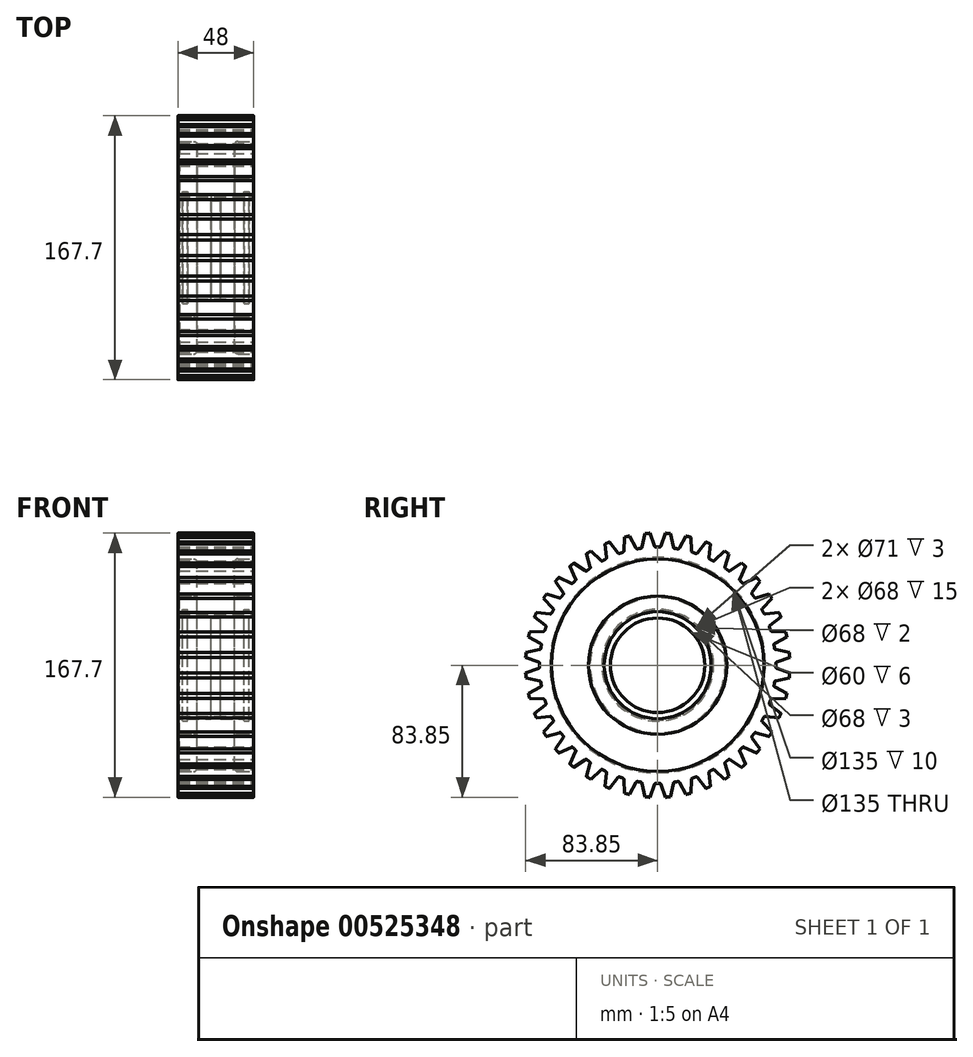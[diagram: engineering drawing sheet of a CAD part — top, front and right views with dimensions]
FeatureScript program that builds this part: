
annotation { "Feature Type Name" : "Feature", "Feature Type Description" : "" }
export const myFeature = defineFeature(function(context is Context, id is Id, definition is map)
    precondition{}
    {
        {
            var Q0;
            Q0=qCreatedBy(makeId("Front.planeOp"),FACE);
            var sketch = newSketch(context, id + "F0", { "sketchPlane" : qUnion([Q0])});
            skLineSegment(sketch, "E0.bottom", {"start": v(0, 0) * mm, "end": v(-24, 0) * mm, "construction": true});
            skLineSegment(sketch, "E0.top", {"start": v(0, 84) * mm, "end": v(-24, 84) * mm});
            skLineSegment(sketch, "E0.left", {"start": v(0, 0) * mm, "end": v(0, 84) * mm, "construction": true});
            skLineSegment(sketch, "E0.right", {"start": v(-24, 34) * mm, "end": v(-24, 44) * mm});
            skLineSegment(sketch, "E1", {"start": v(-24, 34) * mm, "end": v(-21, 34) * mm});
            skLineSegment(sketch, "E2", {"start": v(-21, 34) * mm, "end": v(-21, 35.5) * mm});
            skLineSegment(sketch, "E3", {"start": v(-21, 35.5) * mm, "end": v(-18, 35.5) * mm});
            skLineSegment(sketch, "E4", {"start": v(-18, 35.5) * mm, "end": v(-18, 34) * mm});
            skLineSegment(sketch, "E5", {"start": v(-18, 34) * mm, "end": v(-3, 34) * mm});
            skLineSegment(sketch, "E6", {"start": v(-3, 34) * mm, "end": v(-3, 30) * mm});
            skLineSegment(sketch, "E7", {"start": v(-3, 30) * mm, "end": v(0, 30) * mm});
            skLineSegment(sketch, "E8.bottom", {"start": v(-24, 44) * mm, "end": v(-14, 44) * mm});
            skLineSegment(sketch, "E8.top", {"start": v(-24, 67.5) * mm, "end": v(-14, 67.5) * mm});
            skLineSegment(sketch, "E8.right", {"start": v(-12, 65.5) * mm, "end": v(-12, 46) * mm});
            skLineSegment(sketch, "E9.trimOffspring", {"start": v(-24, 67.5) * mm, "end": v(-24, 84) * mm});
            skPoint(sketch, "E10.visualSharp", {"position": v(-12, 67.5) * mm});
            skArc(sketch, "E10.filletArc", {"start": v(-12, 65.5) * mm, "mid": v(-12.59, 66.91) * mm, "end": v(-14, 67.5) * mm});
            skPoint(sketch, "E11.visualSharp", {"position": v(-12, 44) * mm});
            skArc(sketch, "E11.filletArc", {"start": v(-14, 44) * mm, "mid": v(-12.59, 44.59) * mm, "end": v(-12, 46) * mm});
            skLineSegment(sketch, "E12.MirrorCS", {"start": v(0, 84) * mm, "end": v(24, 84) * mm});
            skLineSegment(sketch, "E13.MirrorCS", {"start": v(24, 67.5) * mm, "end": v(24, 84) * mm});
            skLineSegment(sketch, "E14.MirrorCS", {"start": v(24, 67.5) * mm, "end": v(14, 67.5) * mm});
            skArc(sketch, "E15.MirrorCS", {"start": v(12, 65.5) * mm, "mid": v(12.59, 66.91) * mm, "end": v(14, 67.5) * mm});
            skLineSegment(sketch, "E16.MirrorCS", {"start": v(12, 65.5) * mm, "end": v(12, 46) * mm});
            skArc(sketch, "E17.MirrorCS", {"start": v(14, 44) * mm, "mid": v(12.59, 44.59) * mm, "end": v(12, 46) * mm});
            skLineSegment(sketch, "E18.MirrorCS", {"start": v(24, 44) * mm, "end": v(14, 44) * mm});
            skLineSegment(sketch, "E19.MirrorCS", {"start": v(24, 34) * mm, "end": v(24, 44) * mm});
            skLineSegment(sketch, "E20.MirrorCS", {"start": v(24, 34) * mm, "end": v(21, 34) * mm});
            skLineSegment(sketch, "E21.MirrorCS", {"start": v(21, 35.5) * mm, "end": v(18, 35.5) * mm});
            skLineSegment(sketch, "E22.MirrorCS", {"start": v(18, 34) * mm, "end": v(3, 34) * mm});
            skLineSegment(sketch, "E23.MirrorCS", {"start": v(3, 34) * mm, "end": v(3, 30) * mm});
            skLineSegment(sketch, "E24.MirrorCS", {"start": v(3, 30) * mm, "end": v(0, 30) * mm});
            skLineSegment(sketch, "E25.MirrorCS", {"start": v(18, 35.5) * mm, "end": v(18, 34) * mm});
            skLineSegment(sketch, "E26.MirrorCS", {"start": v(21, 34) * mm, "end": v(21, 35.5) * mm});
            skSolve(sketch);
        }
        {
            var Q0;
            Q0=makeQuery(id+"F0.imprint","IMPRINT",FACE,{"disambiguationData":[TD([[makeQuery(id+"F0.imprint","IMPRINT",EDGE,{"derivedFrom":sQuery(id+"F0.wireOp",EDGE,"E0.top")}),1.0]])]});
            var Q1;
            Q1=sQuery(id+"F0.wireOp",EDGE,"E0.bottom");
            revolve(context, id + "F1", {"entities" : qUnion([Q0]), "axis" : qUnion([Q1]), "revolveType" : RevolveType.FULL});
        }
        {
            var Q0;
            Q0=qCreatedBy(makeId("Right.planeOp"),FACE);
            var sketch = newSketch(context, id + "F2", { "sketchPlane" : qUnion([Q0])});
            skArc(sketch, "E27", {"start": v(1.04, 75) * mm, "mid": v(0, 75) * mm, "end": v(-1.04, 75) * mm});
            skLineSegment(sketch, "E28", {"start": v(0, 0) * mm, "end": v(0, 84) * mm, "construction": true});
            skLineSegment(sketch, "E29", {"start": v(-2, 75.65) * mm, "end": v(-4.98, 83.85) * mm});
            skLineSegment(sketch, "E30.MirrorCS", {"start": v(2, 75.65) * mm, "end": v(4.98, 83.85) * mm});
            skPoint(sketch, "E31.visualSharp", {"position": v(1.75, 74.98) * mm});
            skArc(sketch, "E31.filletArc", {"start": v(1.04, 75) * mm, "mid": v(1.62, 75.17) * mm, "end": v(2, 75.65) * mm});
            skPoint(sketch, "E32.visualSharp", {"position": v(-1.75, 74.98) * mm});
            skArc(sketch, "E32.filletArc", {"start": v(-2, 75.65) * mm, "mid": v(-1.62, 75.17) * mm, "end": v(-1.04, 75) * mm});
            skArc(sketch, "E33", {"start": v(4.98, 83.85) * mm, "mid": v(0, 84) * mm, "end": v(-4.98, 83.85) * mm});
            skSolve(sketch);
        }
        {
            var Q0;
            Q0=qSketchRegion(id+"F2",true);
            extrude(context, id + "F3", {"entities" : qUnion([Q0]), "operationType" : NewBodyOperationType.REMOVE, "endBound" : BoundingType.SYMMETRIC, "oppositeDirection" : true, "depth" : 48.8 * mm, "offsetDistance" : 25 * mm});
        }
        {
            var Q0;
            Q0=makeQuery(id+"F3.boolean.opBoolean","COPY",FACE,{"derivedFrom":makeQuery(id+"F3.opExtrude","SWEPT_FACE",FACE,{"disambiguationData":[OSD([sQuery(id+"F2.wireOp",EDGE,"E30.MirrorCS")])]})});
            var Q1;
            Q1=makeQuery(id+"F3.boolean.opBoolean","COPY",FACE,{"derivedFrom":makeQuery(id+"F3.opExtrude","SWEPT_FACE",FACE,{"disambiguationData":[OSD([sQuery(id+"F2.wireOp",EDGE,"E31.filletArc")])]})});
            var Q2;
            Q2=makeQuery(id+"F3.boolean.opBoolean","COPY",FACE,{"derivedFrom":makeQuery(id+"F3.opExtrude","SWEPT_FACE",FACE,{"disambiguationData":[OSD([sQuery(id+"F2.wireOp",EDGE,"E27")])]})});
            var Q3;
            Q3=makeQuery(id+"F3.boolean.opBoolean","COPY",FACE,{"derivedFrom":makeQuery(id+"F3.opExtrude","SWEPT_FACE",FACE,{"disambiguationData":[OSD([sQuery(id+"F2.wireOp",EDGE,"E32.filletArc")])]})});
            var Q4;
            Q4=makeQuery(id+"F3.boolean.opBoolean","COPY",FACE,{"derivedFrom":makeQuery(id+"F3.opExtrude","SWEPT_FACE",FACE,{"disambiguationData":[OSD([sQuery(id+"F2.wireOp",EDGE,"E29")])]})});
            var Q5;
            Q5=makeQuery(id+"F1.opRevolve","SWEPT_FACE",FACE,{"disambiguationData":[OSD([sQuery(id+"F0.wireOp",EDGE,"E0.top"),sQuery(id+"F0.wireOp",EDGE,"E12.MirrorCS")])]});
            circularPattern(context, id + "F4", {"patternType" : PatternType.FACE, "operationType" : NewBodyOperationType.REMOVE, "faces" : qUnion([Q0, Q1, Q2, Q3, Q4]), "axis" : qUnion([Q5]), "angle" : 360 * degree, "instanceCount" : 40, "equalSpace" : true});
        }
        {
            var Q0;
            Q0=makeQuery(id+"F1.opRevolve","SWEPT_EDGE",EDGE,{"disambiguationData":[OSD([sQuery(id+"F0.wireOp",EDGE,"E8.top"),sQuery(id+"F0.wireOp",EDGE,"E9.trimOffspring")])]});
            var Q1;
            Q1=makeQuery(id+"F1.opRevolve","SWEPT_EDGE",EDGE,{"disambiguationData":[OSD([sQuery(id+"F0.wireOp",EDGE,"E0.right"),sQuery(id+"F0.wireOp",EDGE,"E8.bottom")])]});
            var Q2;
            Q2=makeQuery(id+"F1.opRevolve","SWEPT_EDGE",EDGE,{"disambiguationData":[OSD([sQuery(id+"F0.wireOp",EDGE,"E0.right"),sQuery(id+"F0.wireOp",EDGE,"E1")])]});
            var Q3;
            Q3=makeQuery(id+"F1.opRevolve","SWEPT_EDGE",EDGE,{"disambiguationData":[OSD([sQuery(id+"F0.wireOp",EDGE,"E8.bottom"),sQuery(id+"F0.wireOp",EDGE,"E11.filletArc")])]});
            chamfer(context, id + "F5", {"entities" : qUnion([Q0, Q1, Q2, Q3]), "width" : 1 * mm, "tangentPropagation" : true});
        }
    });
